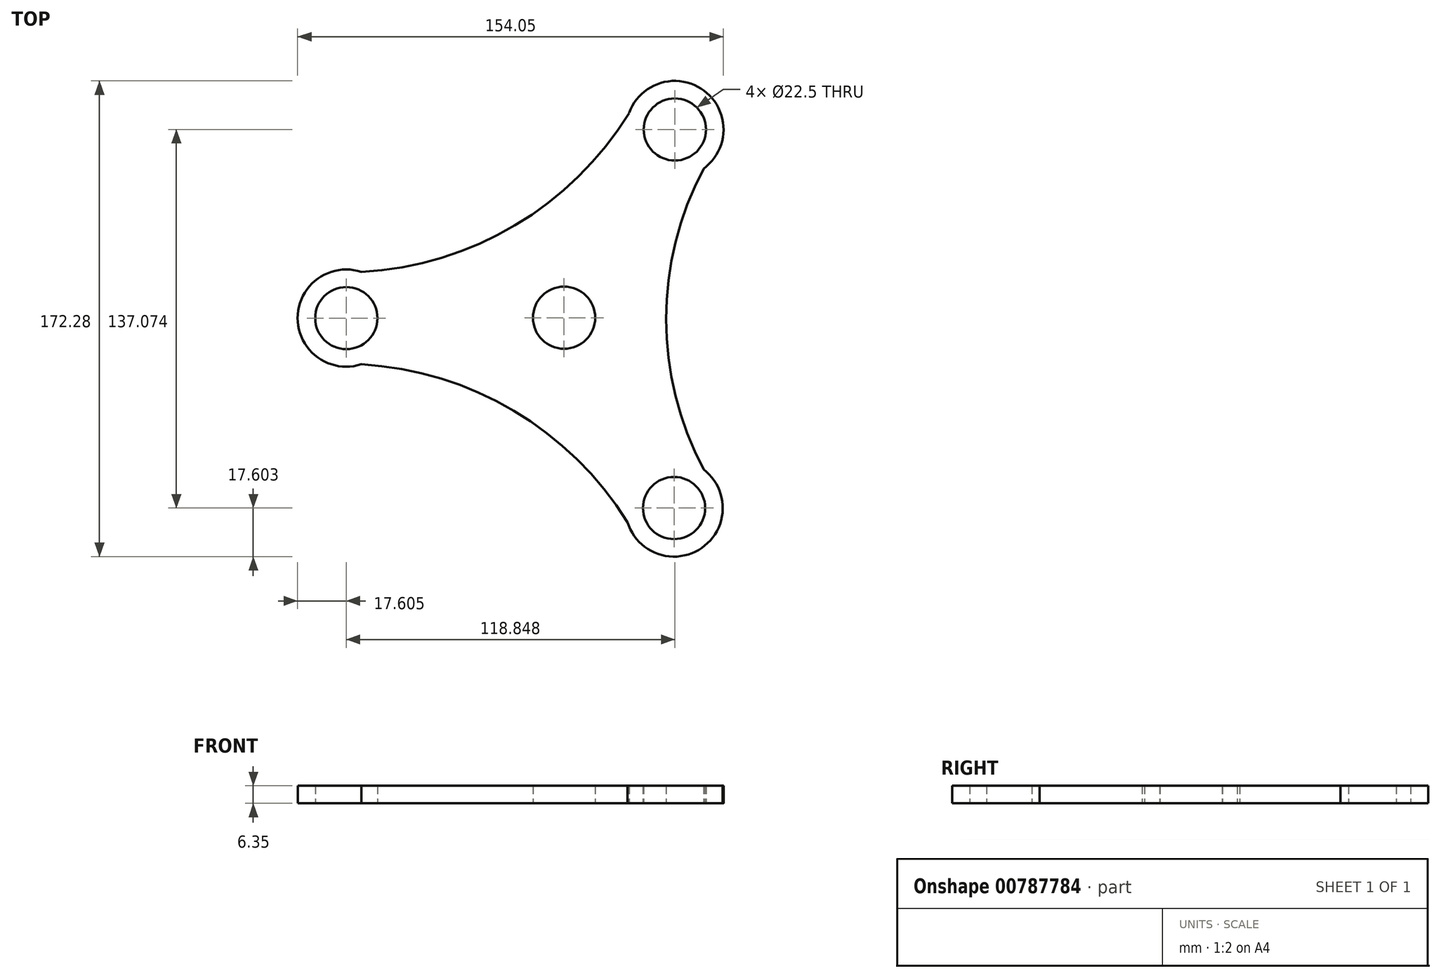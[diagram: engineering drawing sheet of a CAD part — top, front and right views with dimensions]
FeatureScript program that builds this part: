
annotation { "Feature Type Name" : "Feature", "Feature Type Description" : "" }
export const myFeature = defineFeature(function(context is Context, id is Id, definition is map)
    precondition{}
    {
        {
            var Q0;
            Q0=qCreatedBy(makeId("Top.planeOp"),FACE);
            var sketch = newSketch(context, id + "F0", { "sketchPlane" : qUnion([Q0])});
            skCircle(sketch, "E0", {"center": v(-134.28, 16.74) * mm, "radius": 11.25 * mm});
            skArc(sketch, "E1.0", {"start": v(-128.84, 33.48) * mm, "mid": v(-151.89, 16.74) * mm, "end": v(-128.84, 0) * mm});
            skCircle(sketch, "E2", {"center": v(-55.5, 16.88) * mm, "radius": 11.25 * mm});
            skCircle(sketch, "E3.1.0", {"center": v(-15.71, -52.04) * mm, "radius": 11.25 * mm});
            skCircle(sketch, "E3.2.0", {"center": v(-15.44, 85.04) * mm, "radius": 11.25 * mm});
            skPoint(sketch, "E3.center", {"position": v(-55.15, 16.58) * mm});
            skArc(sketch, "E4.0", {"start": v(-32.54, -57.2) * mm, "mid": v(-5.66, -66.48) * mm, "end": v(-5.04, -38.04) * mm});
            skArc(sketch, "E5.0", {"start": v(-5.04, 70.84) * mm, "mid": v(-4.87, 99.11) * mm, "end": v(-31.98, 91.06) * mm});
            skArc(sketch, "E6", {"start": v(-32.54, -57.2) * mm, "mid": v(-73.7, -16.83) * mm, "end": v(-128.84, 0) * mm});
            skArc(sketch, "E7.2.0", {"start": v(-130.4, 33.4) * mm, "mid": v(-73.97, 49.9) * mm, "end": v(-31.98, 91.06) * mm});
            skPoint(sketch, "E7.center", {"position": v(-55.74, 16.57) * mm});
            skArc(sketch, "E8", {"start": v(-5.04, 70.84) * mm, "mid": v(-18.57, 16.4) * mm, "end": v(-5.04, -38.04) * mm});
            skSolve(sketch);
        }
        {
            var Q0;
            Q0 = qSketchRegion(id + "F0", true);
            extrude(context, id + "F1", {"entities" : qUnion([Q0]), "depth" : 6.35 * mm, "offsetDistance" : 25.4 * mm});
        }
    });
